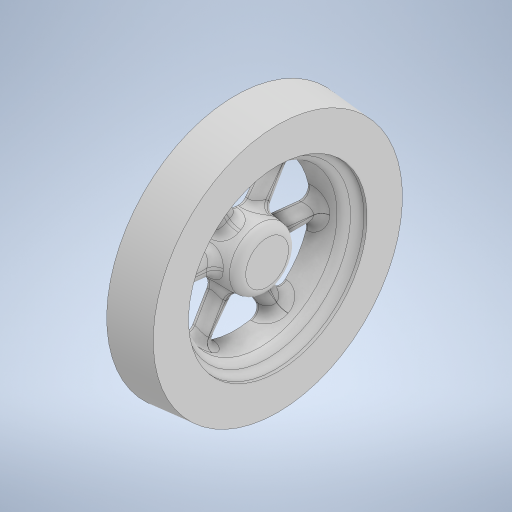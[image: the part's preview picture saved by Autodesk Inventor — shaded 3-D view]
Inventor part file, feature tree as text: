
AUTODESK INVENTOR PART (.ipt)
format: ipt  version: 2023 (Build 270158000, 158)  size: 1,148,416 bytes
history: native  units: in
note: dims shown in document units (in); Inventor stores cm internally (conversion verified against a paired STEP export)
features: extrude x5, sketch x3, fillet x2, draft x1
ambient origin geometry x8: Origin, YZ Plane, XZ Plane, XY Plane, X Axis, Y Axis, Z Axis, Center Point
bodies: Body1 (feature_tree)
feature tree (11):
  sketch  "Sketch1"  dims[d29=0.125in d31=2.0in d32=3.0in]
  extrude  "Extrusion7"  Depth=3.0in
  extrude  "Extrusion8"  Depth=0.25in
  extrude  "Extrusion9"  Depth=0.3in TaperAngle=360.0deg
  sketch  "Sketch3"  dims[d33=0.75in d34=0.25in]
  draft  "FaceDraft2"
  fillet  "Fillet5"  Radius=1.0in
  fillet  "Fillet6"  Radius=0.75in
  extrude  "Extrusion11"  Depth=0.3in TaperAngle=0.0deg
  extrude  "Extrusion12"  Depth=0.3in
  sketch  "Sketch4"  dims[d35=1.75in d37=2.3622in d39=360.0deg d41=1.0in d42=0.0in d43=0.75in d44=0.0in d45=0.25in d46=0.0in d54=0.0344in d55=0.1in d56=0.1in d57=5.0in d58=0.0in d59=0.26in d60=0.26in d61=1.125in d62=1.125in d63=0.26in d64=0.3in d65=0.0in]
